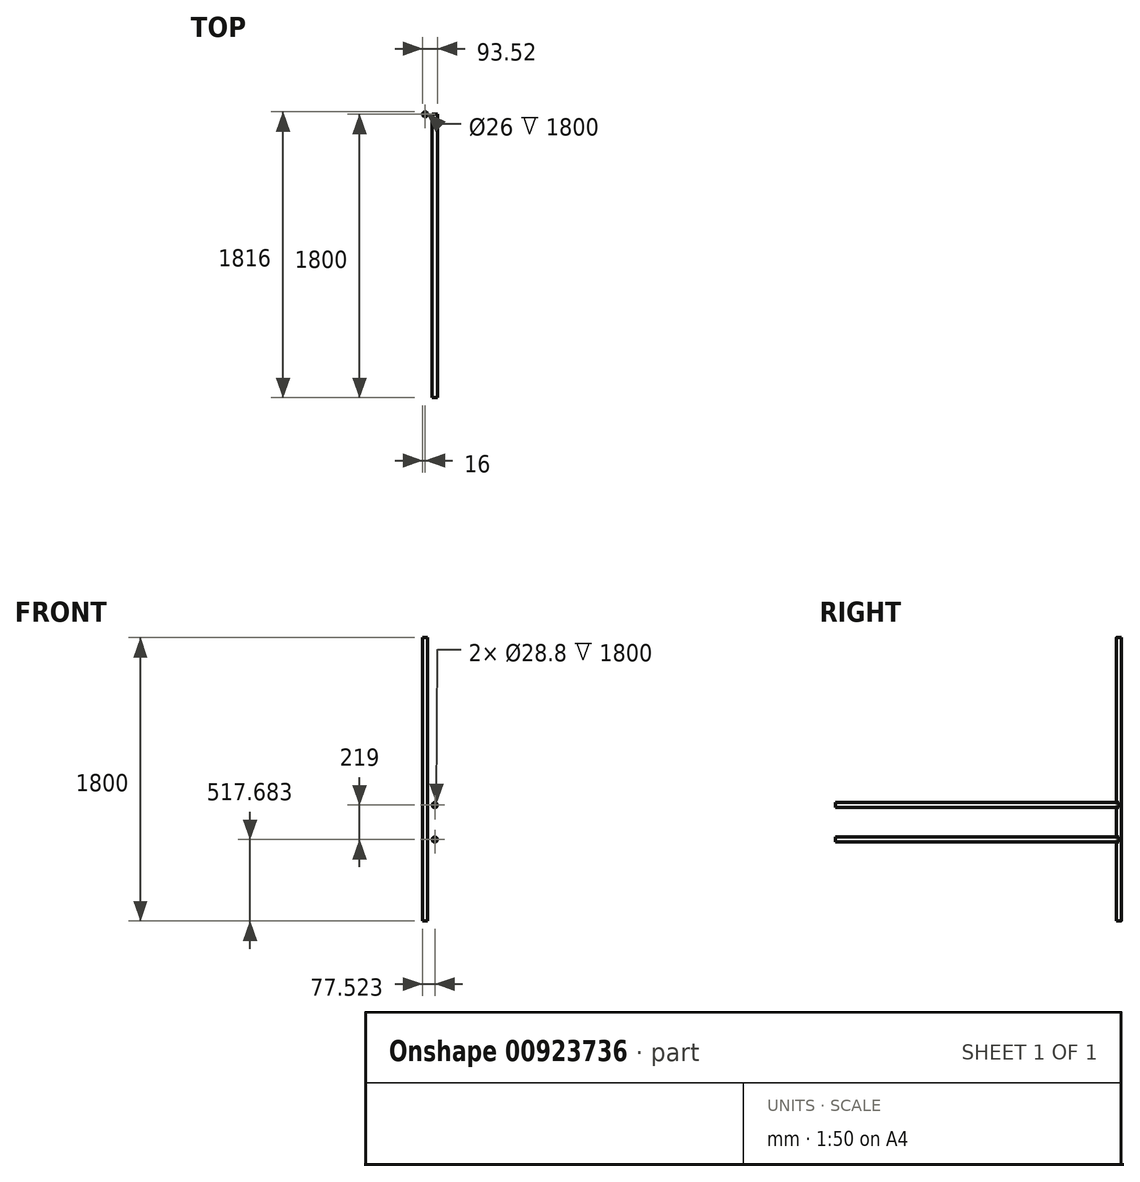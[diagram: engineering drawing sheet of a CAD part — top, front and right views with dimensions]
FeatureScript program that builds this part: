
annotation { "Feature Type Name" : "Feature", "Feature Type Description" : "" }
export const myFeature = defineFeature(function(context is Context, id is Id, definition is map)
    precondition{}
    {
        {
            var Q0;
            Q0=qCreatedBy(makeId("Top.planeOp"),FACE);
            var sketch = newSketch(context, id + "F0", { "sketchPlane" : qUnion([Q0])});
            skCircle(sketch, "E0", {"center": v(0, 0) * mm, "radius": 16 * mm});
            skCircle(sketch, "E1.0", {"center": v(0, 0) * mm, "radius": 13 * mm});
            skSolve(sketch);
        }
        {
            var Q0;
            Q0 = qSketchRegion(id + "F0", true);
            extrude(context, id + "F1", {"entities" : qUnion([Q0]), "depth" : 1800 * mm, "offsetDistance" : 25 * mm});
        }
        {
            var Q0;
            Q0=qCreatedBy(makeId("Front.planeOp"),FACE);
            var sketch = newSketch(context, id + "F2", { "sketchPlane" : qUnion([Q0])});
            skCircle(sketch, "E2", {"center": v(61.52, 517.68) * mm, "radius": 16 * mm});
            skCircle(sketch, "E3.0", {"center": v(61.52, 517.68) * mm, "radius": 14.4 * mm});
            skCircle(sketch, "E4.0.1.0", {"center": v(61.52, 736.68) * mm, "radius": 14.4 * mm});
            skCircle(sketch, "E4.0.1.1", {"center": v(61.52, 736.68) * mm, "radius": 16 * mm});
            skLineSegment(sketch, "E4.direction1", {"start": v(61.52, 517.68) * mm, "end": v(86.52, 517.68) * mm, "construction": true});
            skLineSegment(sketch, "E4.direction2", {"start": v(61.52, 517.68) * mm, "end": v(61.52, 736.68) * mm, "construction": true});
            skSolve(sketch);
        }
        {
            var Q0;
            Q0 = qSketchRegion(id + "F2", true);
            extrude(context, id + "F3", {"entities" : qUnion([Q0]), "depth" : 1800 * mm, "offsetDistance" : 25 * mm});
        }
    });
